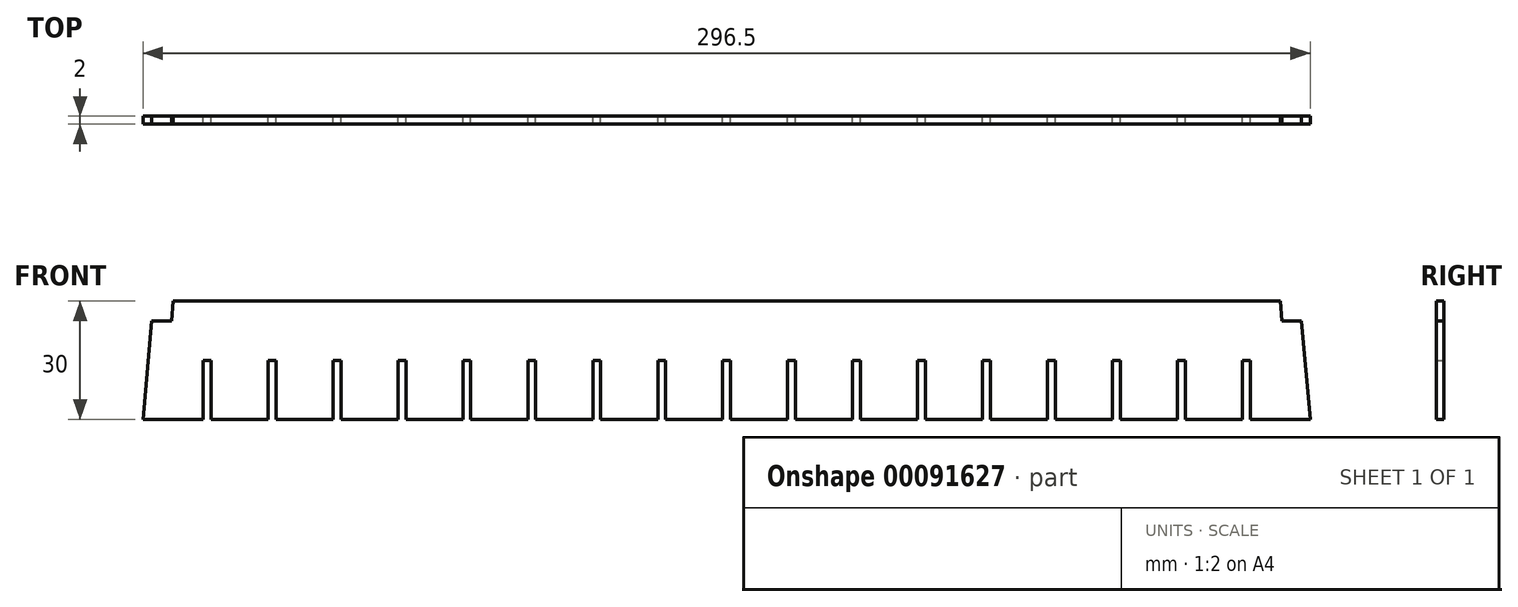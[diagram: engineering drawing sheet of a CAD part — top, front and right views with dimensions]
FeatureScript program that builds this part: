
annotation { "Feature Type Name" : "Feature", "Feature Type Description" : "" }
export const myFeature = defineFeature(function(context is Context, id is Id, definition is map)
    precondition{}
    {
        {
            var Q0;
            Q0=qCreatedBy(makeId("Front.planeOp"),FACE);
            var sketch = newSketch(context, id + "F0", { "sketchPlane" : qUnion([Q0])});
            skLineSegment(sketch, "E0", {"start": v(296.5, 0) * mm, "end": v(294.31, 25) * mm});
            skLineSegment(sketch, "E1", {"start": v(0, 0) * mm, "end": v(15.25, 0) * mm});
            skLineSegment(sketch, "E2", {"start": v(31.75, 0) * mm, "end": v(31.75, 15) * mm});
            skLineSegment(sketch, "E3", {"start": v(31.75, 15) * mm, "end": v(33.75, 15) * mm});
            skLineSegment(sketch, "E4", {"start": v(33.75, 15) * mm, "end": v(33.75, 0) * mm});
            skLineSegment(sketch, "E5", {"start": v(33.75, 0) * mm, "end": v(48.25, 0) * mm});
            skLineSegment(sketch, "E6", {"start": v(48.25, 0) * mm, "end": v(48.25, 15) * mm});
            skLineSegment(sketch, "E7", {"start": v(48.25, 15) * mm, "end": v(50.25, 15) * mm});
            skLineSegment(sketch, "E8", {"start": v(50.25, 15) * mm, "end": v(50.25, 0) * mm});
            skLineSegment(sketch, "E9", {"start": v(50.25, 0) * mm, "end": v(64.75, 0) * mm});
            skLineSegment(sketch, "E10", {"start": v(64.75, 0) * mm, "end": v(64.75, 15) * mm});
            skLineSegment(sketch, "E11", {"start": v(64.75, 15) * mm, "end": v(66.75, 15) * mm});
            skLineSegment(sketch, "E12", {"start": v(66.75, 15) * mm, "end": v(66.75, 0) * mm});
            skLineSegment(sketch, "E13", {"start": v(66.75, 0) * mm, "end": v(81.25, 0) * mm});
            skLineSegment(sketch, "E14", {"start": v(81.25, 0) * mm, "end": v(81.25, 15) * mm});
            skLineSegment(sketch, "E15", {"start": v(81.25, 15) * mm, "end": v(83.25, 15) * mm});
            skLineSegment(sketch, "E16", {"start": v(83.25, 15) * mm, "end": v(83.25, 0) * mm});
            skLineSegment(sketch, "E17", {"start": v(83.25, 0) * mm, "end": v(97.75, 0) * mm});
            skLineSegment(sketch, "E18", {"start": v(97.75, 0) * mm, "end": v(97.75, 15) * mm});
            skLineSegment(sketch, "E19", {"start": v(97.75, 15) * mm, "end": v(99.75, 15) * mm});
            skLineSegment(sketch, "E20", {"start": v(99.75, 15) * mm, "end": v(99.75, 0) * mm});
            skLineSegment(sketch, "E21", {"start": v(99.75, 0) * mm, "end": v(114.25, 0) * mm});
            skLineSegment(sketch, "E22", {"start": v(114.25, 0) * mm, "end": v(114.25, 15) * mm});
            skLineSegment(sketch, "E23", {"start": v(114.25, 15) * mm, "end": v(116.25, 15) * mm});
            skLineSegment(sketch, "E24", {"start": v(116.25, 15) * mm, "end": v(116.25, 0) * mm});
            skLineSegment(sketch, "E25", {"start": v(116.25, 0) * mm, "end": v(130.75, 0) * mm});
            skLineSegment(sketch, "E26", {"start": v(130.75, 0) * mm, "end": v(130.75, 15) * mm});
            skLineSegment(sketch, "E27", {"start": v(130.75, 15) * mm, "end": v(132.75, 15) * mm});
            skLineSegment(sketch, "E28", {"start": v(132.75, 15) * mm, "end": v(132.75, 0) * mm});
            skLineSegment(sketch, "E29", {"start": v(132.75, 0) * mm, "end": v(147.25, 0) * mm});
            skLineSegment(sketch, "E30", {"start": v(147.25, 0) * mm, "end": v(147.25, 15) * mm});
            skLineSegment(sketch, "E31", {"start": v(147.25, 15) * mm, "end": v(149.25, 15) * mm});
            skLineSegment(sketch, "E32", {"start": v(149.25, 15) * mm, "end": v(149.25, 0) * mm});
            skLineSegment(sketch, "E33", {"start": v(149.25, 0) * mm, "end": v(163.75, 0) * mm});
            skLineSegment(sketch, "E34", {"start": v(163.75, 0) * mm, "end": v(163.75, 15) * mm});
            skLineSegment(sketch, "E35", {"start": v(163.75, 15) * mm, "end": v(165.75, 15) * mm});
            skLineSegment(sketch, "E36", {"start": v(165.75, 15) * mm, "end": v(165.75, 0) * mm});
            skLineSegment(sketch, "E37", {"start": v(165.75, 0) * mm, "end": v(180.25, 0) * mm});
            skLineSegment(sketch, "E38", {"start": v(180.25, 0) * mm, "end": v(180.25, 15) * mm});
            skLineSegment(sketch, "E39", {"start": v(180.25, 15) * mm, "end": v(182.25, 15) * mm});
            skLineSegment(sketch, "E40", {"start": v(182.25, 15) * mm, "end": v(182.25, 0) * mm});
            skLineSegment(sketch, "E41", {"start": v(182.25, 0) * mm, "end": v(196.75, 0) * mm});
            skLineSegment(sketch, "E42", {"start": v(196.75, 0) * mm, "end": v(196.75, 15) * mm});
            skLineSegment(sketch, "E43", {"start": v(196.75, 15) * mm, "end": v(198.75, 15) * mm});
            skLineSegment(sketch, "E44", {"start": v(198.75, 15) * mm, "end": v(198.75, 0) * mm});
            skLineSegment(sketch, "E45", {"start": v(198.75, 0) * mm, "end": v(213.25, 0) * mm});
            skLineSegment(sketch, "E46", {"start": v(213.25, 0) * mm, "end": v(213.25, 15) * mm});
            skLineSegment(sketch, "E47", {"start": v(213.25, 15) * mm, "end": v(215.25, 15) * mm});
            skLineSegment(sketch, "E48", {"start": v(215.25, 15) * mm, "end": v(215.25, 0) * mm});
            skLineSegment(sketch, "E49", {"start": v(215.25, 0) * mm, "end": v(229.75, 0) * mm});
            skLineSegment(sketch, "E50", {"start": v(229.75, 0) * mm, "end": v(229.75, 15) * mm});
            skLineSegment(sketch, "E51", {"start": v(229.75, 15) * mm, "end": v(231.75, 15) * mm});
            skLineSegment(sketch, "E52", {"start": v(231.75, 15) * mm, "end": v(231.75, 0) * mm});
            skLineSegment(sketch, "E53", {"start": v(231.75, 0) * mm, "end": v(246.25, 0) * mm});
            skLineSegment(sketch, "E54", {"start": v(246.25, 0) * mm, "end": v(246.25, 15) * mm});
            skLineSegment(sketch, "E55", {"start": v(246.25, 15) * mm, "end": v(248.25, 15) * mm});
            skLineSegment(sketch, "E56", {"start": v(248.25, 15) * mm, "end": v(248.25, 0) * mm});
            skLineSegment(sketch, "E57", {"start": v(248.25, 0) * mm, "end": v(262.75, 0) * mm});
            skLineSegment(sketch, "E58", {"start": v(262.75, 0) * mm, "end": v(262.75, 15) * mm});
            skLineSegment(sketch, "E59", {"start": v(262.75, 15) * mm, "end": v(264.75, 15) * mm});
            skLineSegment(sketch, "E60", {"start": v(264.75, 15) * mm, "end": v(264.75, 0) * mm});
            skLineSegment(sketch, "E61", {"start": v(264.75, 0) * mm, "end": v(279.25, 0) * mm});
            skLineSegment(sketch, "E62", {"start": v(279.25, 0) * mm, "end": v(279.25, 15) * mm});
            skLineSegment(sketch, "E63", {"start": v(279.25, 15) * mm, "end": v(281.25, 15) * mm});
            skLineSegment(sketch, "E64", {"start": v(281.25, 15) * mm, "end": v(281.25, 0) * mm});
            skLineSegment(sketch, "E65", {"start": v(281.25, 0) * mm, "end": v(296.5, 0) * mm});
            skLineSegment(sketch, "E66", {"start": v(294.31, 25) * mm, "end": v(289.31, 25) * mm});
            skLineSegment(sketch, "E67", {"start": v(289.31, 25) * mm, "end": v(288.88, 30) * mm});
            skLineSegment(sketch, "E68", {"start": v(288.88, 30) * mm, "end": v(7.62, 30) * mm});
            skLineSegment(sketch, "E69", {"start": v(7.62, 30) * mm, "end": v(7.19, 25) * mm});
            skLineSegment(sketch, "E70", {"start": v(7.19, 25) * mm, "end": v(2.19, 25) * mm});
            skLineSegment(sketch, "E71", {"start": v(2.19, 25) * mm, "end": v(0, 0) * mm});
            skLineSegment(sketch, "E72", {"start": v(17.25, 0) * mm, "end": v(31.75, 0) * mm});
            skLineSegment(sketch, "E73", {"start": v(15.25, 0) * mm, "end": v(15.25, 15) * mm});
            skLineSegment(sketch, "E74", {"start": v(15.25, 15) * mm, "end": v(17.25, 15) * mm});
            skLineSegment(sketch, "E75", {"start": v(17.25, 15) * mm, "end": v(17.25, 0) * mm});
            skSolve(sketch);
        }
        {
            var Q0;
            Q0 = qSketchRegion(id + "F0", true);
            extrude(context, id + "F1", {"entities" : qUnion([Q0]), "depth" : 2 * mm});
        }
    });
